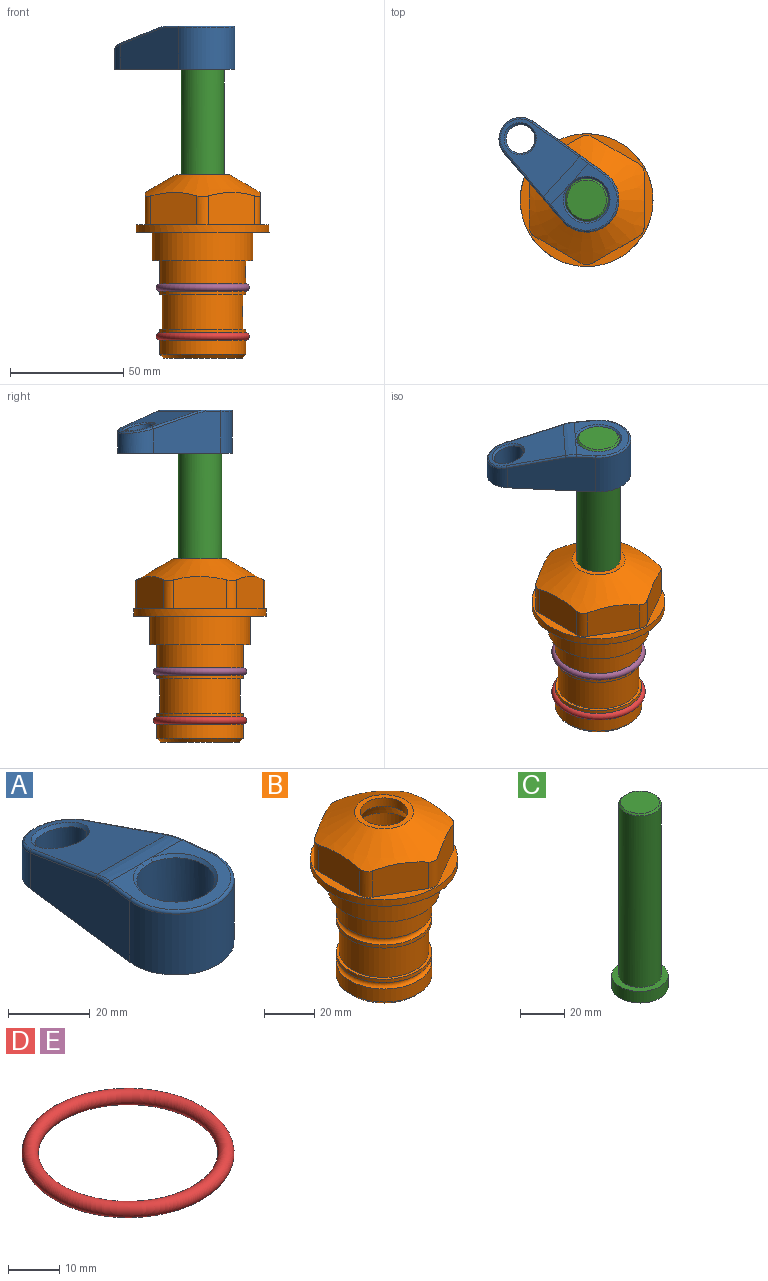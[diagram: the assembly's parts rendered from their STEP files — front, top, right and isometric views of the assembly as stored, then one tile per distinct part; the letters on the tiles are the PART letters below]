
ASSEMBLY  parts=5 mates=4
PART A: 31 faces, bbox 31.7x65.5x19.8 mm
  f0: plane 39.12x18.26mm, normal (0.99,0.12,0), area 612.2mm2, adj f1,f4,f7,f11,f13,f15
  f1: cylinder r=9.53mm len=18.91mm, axis (0,0,-1), area 296.1mm2, adj f0,f2,f7,f17
  f2: plane 39.12x18.26mm, normal (-0.99,0.12,0), area 612.2mm2, adj f1,f4,f7,f12,f14,f16
  f3: cylinder r=6.35mm len=12.7mm, axis (0,0,-1), area 362.4mm2, adj f7,f18
  f4: cylinder r=14.29mm len=28.58mm, axis (0,0,-1), area 882.2mm2, adj f0,f2,f7,f10
  f5: cylinder r=9.53mm len=19.05mm, axis (0,0,-1), area 1092.6mm2, adj f7,f19,f20
  f6: plane 26.99x23.69mm, normal (0,0,1), area 216.2mm2, adj f9,f10,f11,f12,f19
  f7: plane 63.5x28.58mm, normal (0,0,-1), area 661.8mm2, adj f0,f1,f2,f3,f4,f5,f22,f23
  f8: plane 33.52x23.6mm, normal (0,0.26,0.97), area 486mm2, adj f9,f15,f16,f17,f18
  f9: cylinder r=19.05mm len=24.72mm, axis (1,0,0), area 120.4mm2, adj f6,f8,f13,f14,f20
  f10: torus R=13.49mm, axis (0,0,1), area 59mm2, adj f4,f6,f11,f12
  f11: cylinder r=0.79mm len=8.67mm, axis (0.12,-0.99,0), area 10.8mm2, adj f0,f6,f10,f13
  f12: cylinder r=0.79mm len=8.67mm, axis (0.12,0.99,0), area 10.8mm2, adj f2,f6,f10,f14
  f13: bspline ~4.95x1.42mm, area 6.1mm2, adj f0,f9,f11,f15
  f14: bspline ~4.95x1.42mm, area 6.1mm2, adj f2,f9,f12,f16
  f15: cylinder r=0.79mm len=25.95mm, axis (0.12,-0.96,0.26), area 32.9mm2, adj f0,f8,f13,f17
  f16: cylinder r=0.79mm len=25.95mm, axis (0.12,0.96,-0.26), area 32.9mm2, adj f2,f8,f14,f17
  f17: bspline ~18.91x8.38mm, area 30mm2, adj f1,f8,f15,f16
  f18: bspline ~14.29x14.29mm, area 48.3mm2, adj f3,f8
  f19: cone r=9.53mm half-angle=45deg, axis (0,0,1), area 66.5mm2, adj f5,f6,f20
  f20: bspline ~3.22x0.96mm, area 3.5mm2, adj f5,f9,f19
  f21: plane 2.75x2.72mm, normal (0,0,-1), area 2.9mm2, adj f23,f25,f28
  f22: plane 23.05x15.88mm, normal (-0.99,-0.12,0), area 323.6mm2, adj f7,f25,f26,f27,f28,f29
  f23: plane 23.05x15.88mm, normal (0.99,-0.12,0), area 323.6mm2, adj f7,f21,f25,f27,f28,f30
  f24: cylinder r=9.53mm len=10.69mm, axis (0,0,-1), area 114.7mm2, adj f7,f27,f29,f30
  f25: cylinder r=12.7mm len=20.59mm, axis (0,0,-1), area 381.1mm2, adj f7,f21,f22,f23,f26,f28
  f26: plane 2.75x2.72mm, normal (0,0,-1), area 2.9mm2, adj f22,f25,f28
  f27: plane 19.72x18.37mm, normal (0,-0.26,-0.97), area 291.8mm2, adj f22,f23,f24,f28,f29,f30
  f28: cylinder r=15.88mm len=19.92mm, axis (1,0,0), area 54.8mm2, adj f21,f22,f23,f25,f26,f27
  f29: cylinder r=1.59mm len=11mm, axis (0,0,-1), area 34.7mm2, adj f7,f22,f24,f27
  f30: cylinder r=1.59mm len=11mm, axis (0,0,-1), area 34.7mm2, adj f7,f23,f24,f27
PART B: 36 faces, bbox 58.7x58.7x81 mm
  f0: cylinder r=17.78mm len=35.56mm, axis (0,0,1), area 1670.8mm2, adj f23,f24,f31
  f1: cylinder r=19.05mm len=38.1mm, axis (0,0,1), area 1191.9mm2, adj f26,f27,f30
  f2: plane 58.66x58.66mm, normal (0,0,-1), area 1150.6mm2, adj f3,f28
  f3: cylinder r=29.33mm len=58.66mm, axis (0,0,-1), area 585.1mm2, adj f2,f4
  f4: plane 58.66x58.66mm, normal (0,0,1), area 475.9mm2, adj f3,f5,f6,f7,f8,f9,f10,f11
  f5: plane 20.32x14.34mm, normal (-0.5,0.87,0), area 324.4mm2, adj f4,f15,f16,f17
  f6: plane 20.32x14.34mm, normal (0.5,0.87,0), area 324.4mm2, adj f4,f14,f15,f17
  f7: plane 23.48x14.34mm, normal (1,0,0), area 324.4mm2, adj f4,f13,f14,f17
  f8: plane 20.32x14.34mm, normal (0.5,-0.87,0), area 324.4mm2, adj f4,f12,f13,f17
  f9: plane 20.32x14.34mm, normal (-0.5,-0.87,0), area 324.4mm2, adj f4,f11,f12,f17
  f10: plane 23.48x14.34mm, normal (-1,0,0), area 324.4mm2, adj f4,f11,f16,f17
  f11: cylinder r=5.08mm len=12.85mm, axis (0,0,-1), area 67.2mm2, adj f4,f9,f10,f17
  f12: cylinder r=5.08mm len=12.85mm, axis (0,0,-1), area 67.2mm2, adj f4,f8,f9,f17
  f13: cylinder r=5.08mm len=12.85mm, axis (0,0,-1), area 67.2mm2, adj f4,f7,f8,f17
  f14: cylinder r=5.08mm len=12.85mm, axis (0,0,-1), area 67.2mm2, adj f4,f6,f7,f17
  f15: cylinder r=5.08mm len=12.85mm, axis (0,0,-1), area 67.2mm2, adj f4,f5,f6,f17
  f16: cylinder r=5.08mm len=12.85mm, axis (0,0,-1), area 67.2mm2, adj f4,f5,f10,f17
  f17: cone r=11.73mm half-angle=60deg, axis (0,0,-1), area 2071.8mm2, adj f5,f6,f7,f8,f9,f10,f11,f12
  f18: plane 23.46x23.46mm, normal (0,0,1), area 147.4mm2, adj f17,f35
  f19: plane 34.93x34.93mm, normal (0,0,-1), area 958mm2, adj f29
  f20: cylinder r=19.05mm len=38.1mm, axis (0,0,1), area 760.1mm2, adj f21,f29
  f21: torus R=19.05mm, axis (0,0,1), area 565.3mm2, adj f20,f22
  f22: cylinder r=19.05mm len=38.1mm, axis (0,0,1), area 190mm2, adj f21,f23
  f23: plane 38.1x38.1mm, normal (0,0,1), area 146.9mm2, adj f0,f22
  f24: plane 38.1x38.1mm, normal (0,0,-1), area 146.9mm2, adj f0,f25
  f25: cylinder r=19.05mm len=38.1mm, axis (0,0,1), area 190mm2, adj f24,f26
  f26: torus R=19.05mm, axis (0,0,1), area 565.3mm2, adj f1,f25
  f27: plane 44.45x44.45mm, normal (0,0,-1), area 411.7mm2, adj f1,f28
  f28: cylinder r=22.23mm len=44.45mm, axis (0,0,1), area 1773.5mm2, adj f2,f27
  f29: cone r=19.05mm half-angle=45deg, axis (0,0,1), area 257.5mm2, adj f19,f20
  f30: cylinder r=3.17mm len=6.75mm, axis (-1,0,0), area 128mm2, adj f1,f33
  f31: cylinder r=3.17mm len=6.35mm, axis (-1,0,0), area 102.5mm2, adj f0,f33
  f32: plane 25.4x25.4mm, normal (0,0,1), area 506.7mm2, adj f33
  f33: cylinder r=12.7mm len=66.42mm, axis (0,0,-1), area 5236.2mm2, adj f30,f31,f32,f34
  f34: cone r=9.53mm half-angle=30deg, axis (0,0,-1), area 443.4mm2, adj f33,f35
  f35: cylinder r=9.53mm len=19.05mm, axis (0,0,-1), area 240.9mm2, adj f18,f34
PART C: 6 faces, bbox 25.4x25.4x101.6 mm
  f0: plane 17.46x17.46mm, normal (0,0,1), area 239.5mm2, adj f5
  f1: plane 25.4x25.4mm, normal (0,0,-1), area 506.7mm2, adj f2
  f2: cylinder r=12.7mm len=25.4mm, axis (0,0,1), area 506.7mm2, adj f1,f3
  f3: plane 25.4x25.4mm, normal (0,0,1), area 221.7mm2, adj f2,f4
  f4: cylinder r=9.53mm len=94.46mm, axis (0,0,1), area 5653mm2, adj f3,f5
  f5: cone r=8.73mm half-angle=45deg, axis (0,0,-1), area 64.4mm2, adj f0,f4
PART D: 1 faces, bbox 44.7x44.7x3.2 mm
  f0: torus R=19.05mm, axis (0,0,1), area 1193.9mm2
PART E: same geometry as D
PLACE A rot(axis=(0,0,1),47.4deg) t=(0,0,27.55)mm
PLACE B at identity fixed
PLACE C rot(axis=(0,0,1),47.4deg) t=(0,0,27.55)mm
PLACE D t=(0,0,-21.59)mm
PLACE E at identity
MATE fastened C.f2 <-> A.f4  axis (0,0,1) through (0,0,91.05)mm
MATE fastened D.f0 <-> B.f0  axis (0,0,1) through (0,0,-46.1)mm
MATE cylindrical C.f2 <-> B.f0  axis (0,0,-1) through (0,0,-10.55)mm
MATE fastened E.f0 <-> B.f0  axis (0,0,1) through (0,0,-24.51)mm
